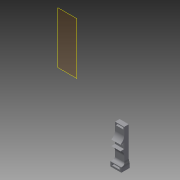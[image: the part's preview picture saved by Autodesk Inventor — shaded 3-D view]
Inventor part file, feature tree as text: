
AUTODESK INVENTOR PART (.ipt)
format: ipt  version: 2015 (Build 190159000, 159)  size: 225,280 bytes
history: native  units: in
note: dims shown in document units (in); Inventor stores cm internally (conversion verified against a paired STEP export)
features: extrude x7, sketch x7, projected_geometry x5, fillet x3, reference x2, plane x1
ambient origin geometry x8: Origin, YZ Plane, XZ Plane, XY Plane, X Axis, Y Axis, Z Axis, Center Point
bodies: Solid1 (feature_tree)
feature tree (25):
  plane  "Work Plane1"
  extrude  "Extrusion1"  Depth=0.5in TaperAngle=0.0deg
  extrude  "Extrusion2"  Depth=0.125in
  extrude  "Extrusion3"  Depth=0.125in
  extrude  "Extrusion4"  Depth=0.5in TaperAngle=0.0deg
  extrude  "Extrusion5"  Depth=0.2in
  extrude  "Extrusion6"  Depth=0.5in TaperAngle=0.0deg
  fillet  "Fillet1"  Radius=0.5in
  extrude  "Extrusion7"  Depth=0.3125in
  fillet  "Fillet2"  Radius=0.125in
  fillet  "Fillet3"  Radius=0.5in
  sketch  "Sketch1"  dims[d2=0.5in d3=0.0in d4=0.1in d5=0.0in]
  reference  "Reference1"
  reference  "Reference2"
  sketch  "Sketch2"  dims[d6=0.125in d9=0.125in]
  sketch  "Sketch3"  dims[d10=0.125in d11=0.125in]
  projected_geometry  "Projected Loop1"
  sketch  "Sketch4"  dims[d12=0.625in d13=0.0in d14=0.5in d15=0.0in]
  projected_geometry  "Projected Loop2"
  sketch  "Sketch5"  dims[d16=0.75in d17=0.2in]
  projected_geometry  "Projected Loop3"
  sketch  "Sketch6"  dims[d18=0.2in d19=0.5in d20=0.0in d21=0.5in d22=0.0in]
  projected_geometry  "Projected Loop4"
  sketch  "Sketch7"  dims[d23=0.875in d24=0.125in d25=0.125in d26=0.5in d27=0.0in d28=0.875in d29=0.3125in]
  projected_geometry  "Projected Loop5"
